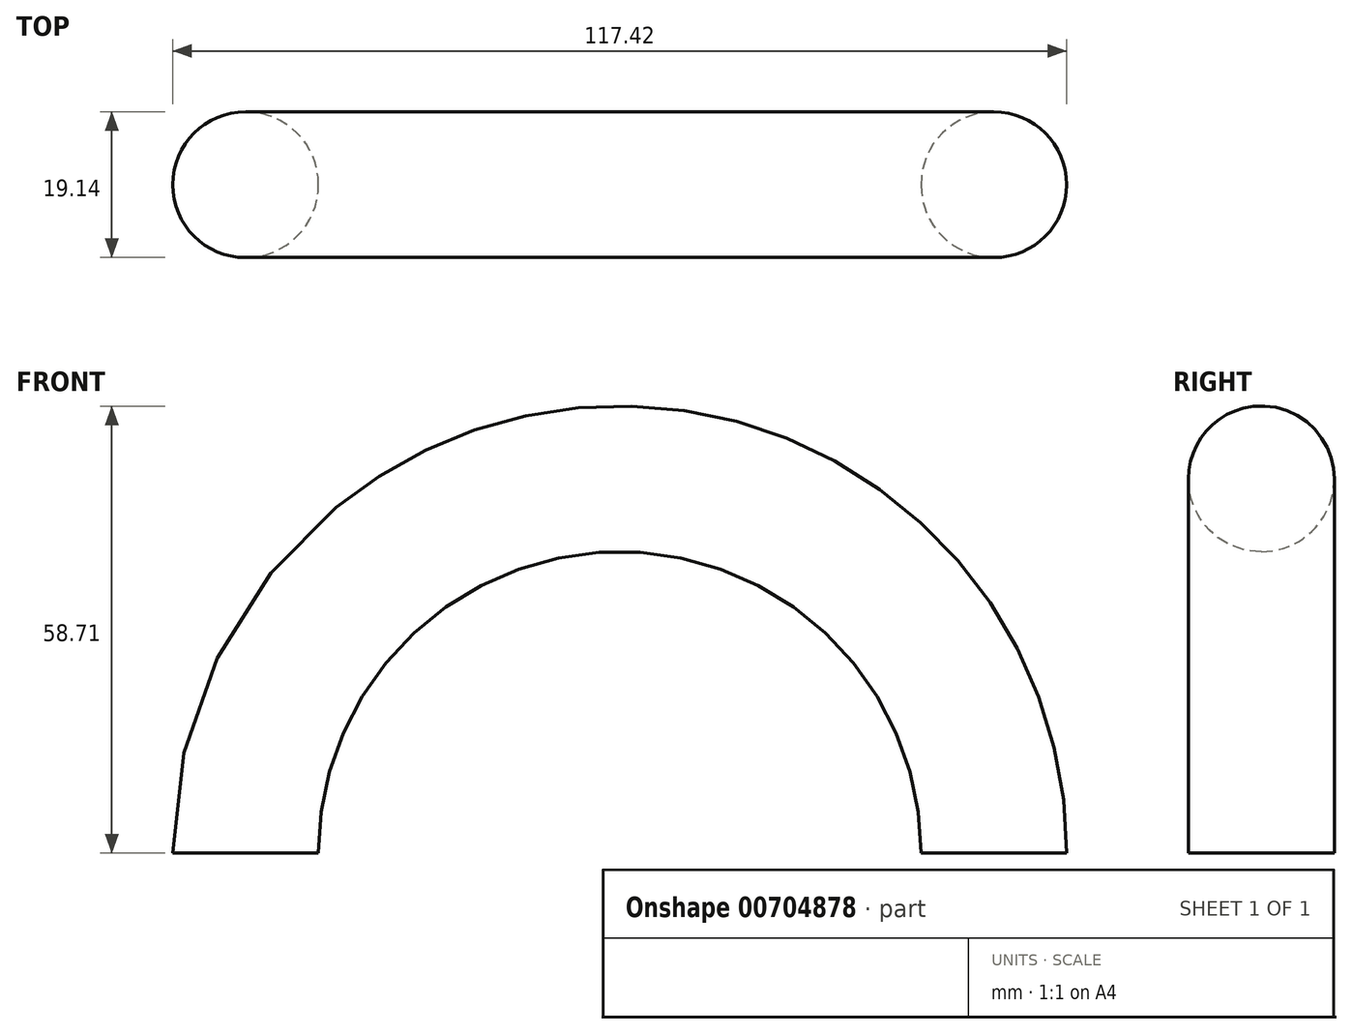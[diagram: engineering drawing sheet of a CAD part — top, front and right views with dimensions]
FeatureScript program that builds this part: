
annotation { "Feature Type Name" : "Feature", "Feature Type Description" : "" }
export const myFeature = defineFeature(function(context is Context, id is Id, definition is map)
    precondition{}
    {
        {
            var Q0;
            Q0=qCreatedBy(makeId("Top.planeOp"),FACE);
            var sketch = newSketch(context, id + "F0", { "sketchPlane" : qUnion([Q0])});
            skCircle(sketch, "E0", {"center": v(-49.14, 0) * mm, "radius": 9.57 * mm});
            skLineSegment(sketch, "E1", {"start": v(0, 32.19) * mm, "end": v(0, -32.53) * mm, "construction": true});
            skCircle(sketch, "E2.MirrorC", {"center": v(49.14, 0) * mm, "radius": 9.57 * mm});
            skSolve(sketch);
        }
        {
            var Q0;
            Q0=makeQuery(id+"F0.imprint","IMPRINT",FACE,{"disambiguationData":[TD([[makeQuery(id+"F0.imprint","IMPRINT",EDGE,{"derivedFrom":sQuery(id+"F0.wireOp",EDGE,"E0")}),1.0]])]});
            var Q1;
            Q1=sQuery(id+"F0.wireOp",EDGE,"E1");
            revolve(context, id + "F1", {"surfaceOperationType" : NewSurfaceOperationType.NEW, "entities" : qUnion([Q0]), "axis" : qUnion([Q1]), "revolveType" : RevolveType.ONE_DIRECTION, "oppositeDirection" : true, "angle" : 180 * degree});
        }
    });
